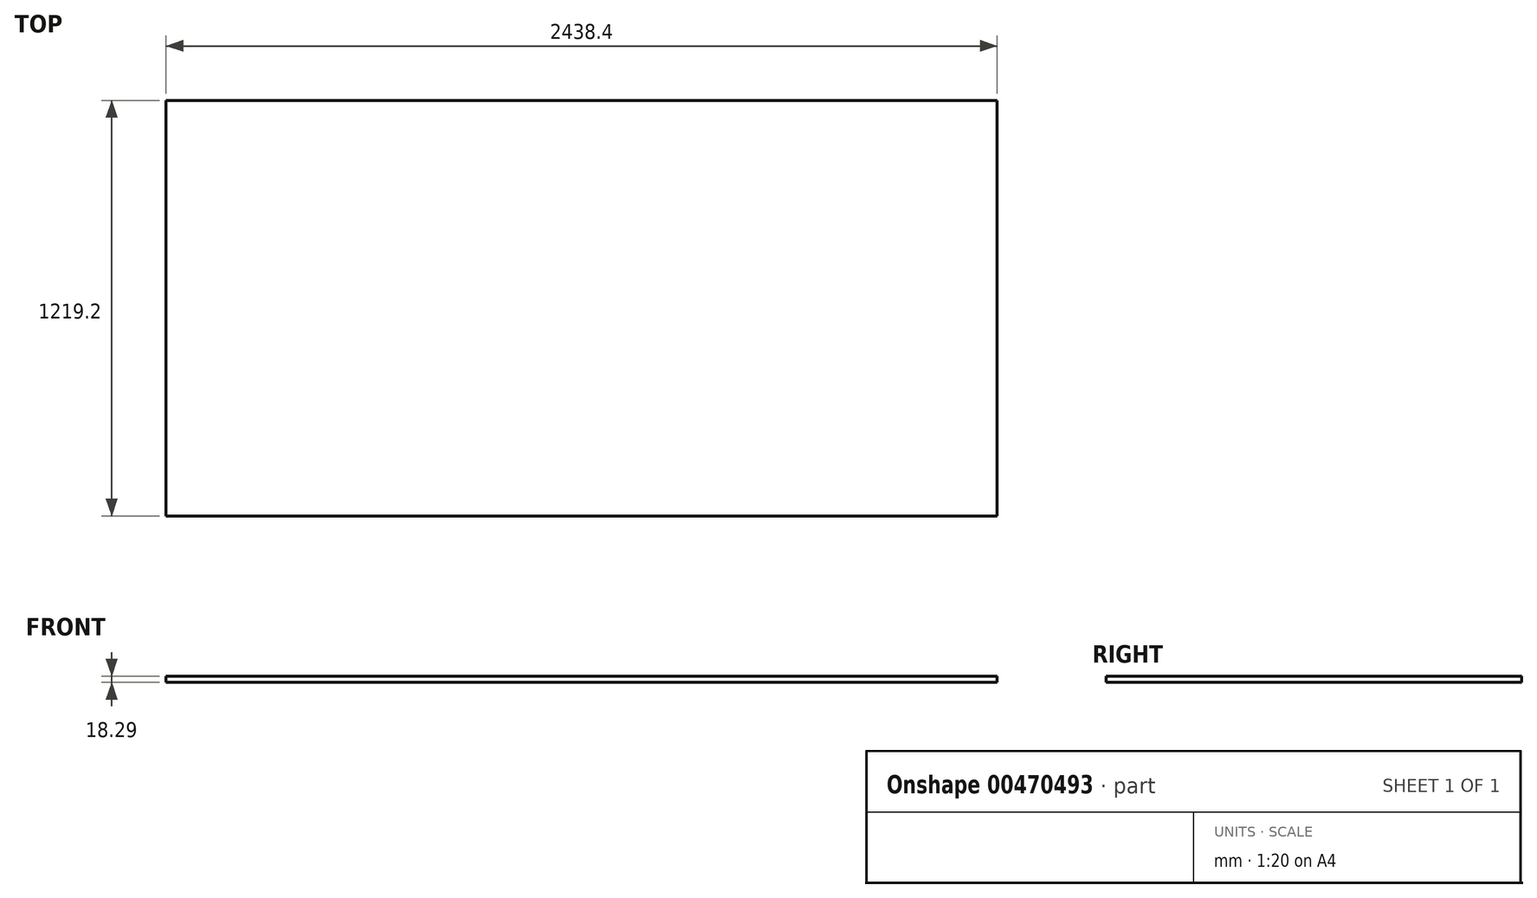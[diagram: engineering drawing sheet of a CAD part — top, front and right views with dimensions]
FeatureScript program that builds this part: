
annotation { "Feature Type Name" : "Feature", "Feature Type Description" : "" }
export const myFeature = defineFeature(function(context is Context, id is Id, definition is map)
    precondition{}
    {
        {
            var Q0;
            Q0=qCreatedBy(makeId("Top.planeOp"),FACE);
            var sketch = newSketch(context, id + "F0", { "sketchPlane" : qUnion([Q0])});
            skLineSegment(sketch, "E0.bottom", {"start": v(0, 0) * mm, "end": v(2438.4, 0) * mm});
            skLineSegment(sketch, "E0.top", {"start": v(0, 1219.2) * mm, "end": v(2438.4, 1219.2) * mm});
            skLineSegment(sketch, "E0.left", {"start": v(0, 0) * mm, "end": v(0, 1219.2) * mm});
            skLineSegment(sketch, "E0.right", {"start": v(2438.4, 0) * mm, "end": v(2438.4, 1219.2) * mm});
            skSolve(sketch);
        }
        {
            var Q0;
            Q0 = qSketchRegion(id + "F0", true);
            extrude(context, id + "F1", {"entities" : qUnion([Q0]), "depth" : 18.29 * mm, "offsetDistance" : 25.4 * mm});
        }
    });
